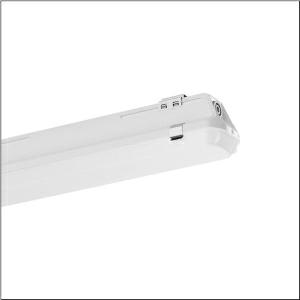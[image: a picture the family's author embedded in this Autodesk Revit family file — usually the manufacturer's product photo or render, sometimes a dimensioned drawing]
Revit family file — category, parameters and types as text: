
# Revit family: monsun_r__21_51fb10mp480b_b142
name_source: partatom
category: Lighting Fixtures
units: mm (PartAtom-declared; Revit-internal decimal feet)

## family parameters
Cut with Voids When Loaded = No
Host = Face
Light Source = No
Part Type = Normal
Room Calculation Point = No
Round Connector Dimension = Use Diameter
Shared = No

## types (1)
- --- (1 x LED, 8190 lm, 53.6 W, 4000K)
    Apparent Load = 54 VA
    CIE Flux Codes = 47 77 93 94 100
    Color Rendering = 80
    Color Temperature = 4000K
    Default Elevation = 1800 mm
    Description = Monsun® 21, damp-proof luminaire, chain hanger, primary optical cover: enclosure, of PMMA, light emission: direct distribution, primary light characteristic: symmetric, installation type: suspended mounting, surface-mounted, horizontal mounting, vertical mounting, LED, rated luminous flux: 8.190lm, luminous efficacy: 153lm/W, light colour: 840, colour temperature: 4000K, control gear: ECG, with terminal, 3-pole, max. 2.5mm², mains connection: 220..240V, AC, 50/60Hz, rated input power: 54W, housing, of glass-fibre reinforced polyester, uncoated, bright grey, incl. chain hanger, length: 1.590mm, width: 90mm, height: 88mm, clip for enclosure, of stainless steel (V2A), ceiling mounting element, of stainless steel (V2A), chain hanger, of stainless steel (V2A), protection rating (complete): IP66, insulation class (complete): insulation class I (protective earthing), certification: CE, ENEC, VDE, UKCA, protection symbol: D, impact resistance: IK04, permissible operating ambient temperature: -25..+35°C, standard: EN 50419, EN 60598-2-1, corresponds to IFS (International Featured Standards) requirements for safety and quality in the food industry, for indoor or canopied outdoor use, no direct snow, no direct sun, no direct rain, contact your sales advisor before using the luminaires in applications with unclear chemical exposure, large temperature fluctuations or condensation-forming humidity, LABS conformity tested according to VDMA 24364:2018-05, packaging unit: 1 piece
    Height = 89 mm
    Lamp = 1 x LED
    Lamp Light Flux = 8190 lm
    Lamp Power = 53.6 W
    Lamp count = 1
    Length = 1590 mm
    Luminous efficacy = 153 lm/W
    Manufacturer = Siteco
    ModVariant = No
    Model = 51FB10MP480B
    Mounting Place = Ceiling
    Mounting Type = Surface mounted
    Number of Poles = 1
    OnlyDefault = Yes
    Power Factor = 1
    Product Name = Monsun® 21
    Product group = damp-proof luminaire
    ProductGroupID = 300
    Protection Class = Protection class I
    Protection Degree = IP 66
    RLX_Detail_Level = 1
    RLX_Emergency_Light_Flux = 0 lm
    RLX_Emergency_Type = 0
    RLX_Emergency_Type_DB = No
    RlxData = <blob elided: 89837 chars, md5=98796ff4>
    Socket = socket
    Standby Power = 0 W
    System Light Flux = 8190 lm
    System Power = 54 W
    Type Comments = factory setting: luminous flux: 100 % | (A | C | E) | 121 mA
    Type Image = l_1319656.jpg
    URL = http://relux.com
    VarID = @adj_117159
    Voltage = 0 V
    Weight = 0.00 kg
    Width = 90 mm

## geometry (parser evidence)
native form markers: Blend x4, Sweep x13
no freeform markers — native parametric forms only
